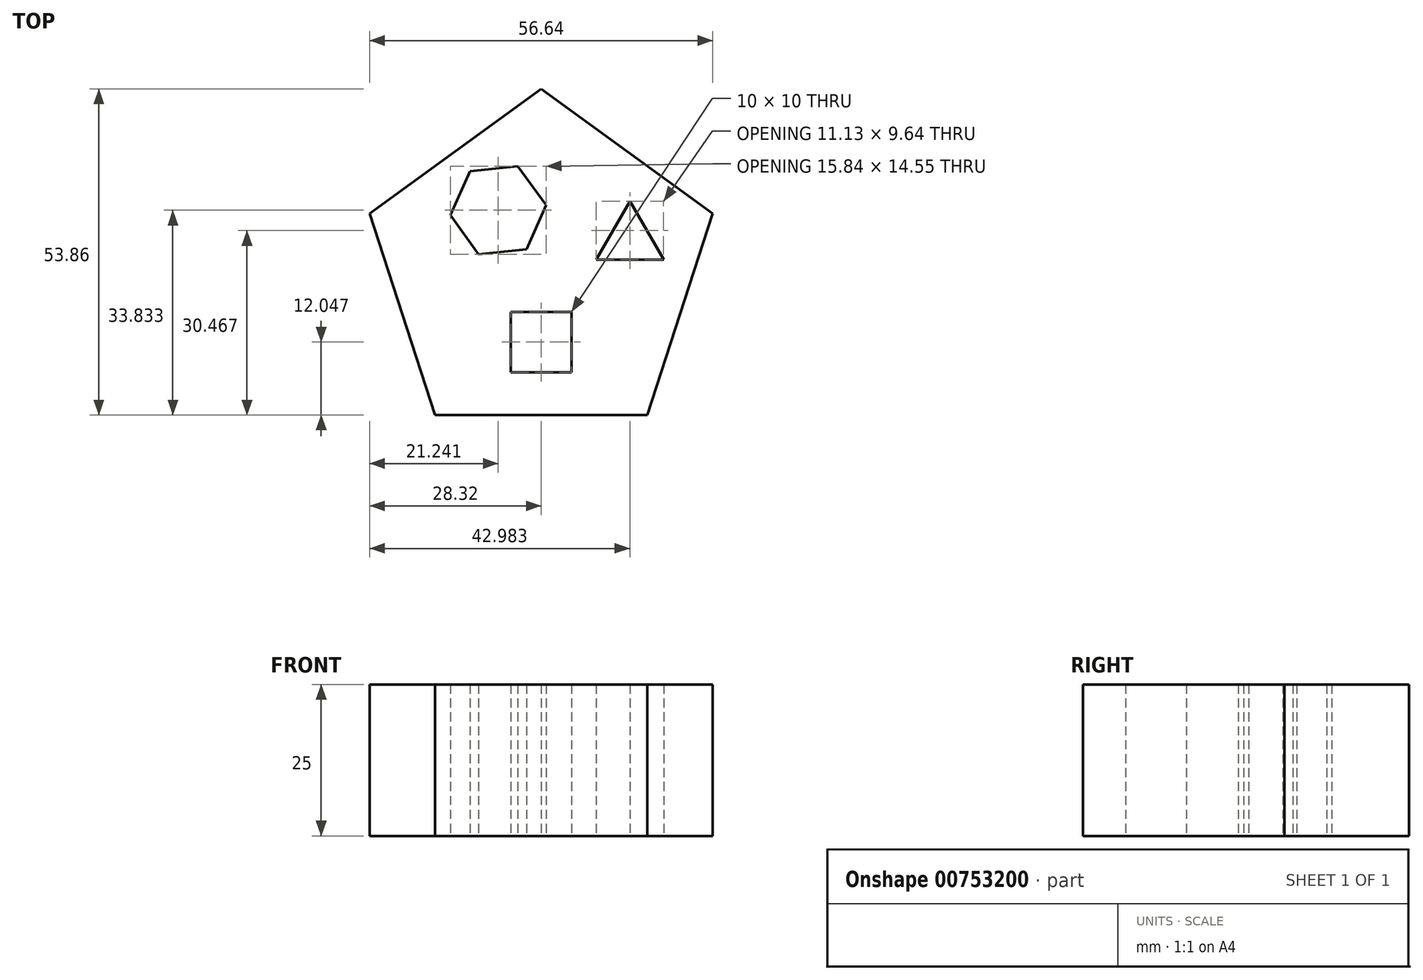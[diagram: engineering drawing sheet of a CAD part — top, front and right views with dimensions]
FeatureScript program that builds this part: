
annotation { "Feature Type Name" : "Feature", "Feature Type Description" : "" }
export const myFeature = defineFeature(function(context is Context, id is Id, definition is map)
    precondition{}
    {
        {
            var Q0;
            Q0=qCreatedBy(makeId("Top.planeOp"),FACE);
            var sketch = newSketch(context, id + "F0", { "sketchPlane" : qUnion([Q0])});
            skCircle(sketch, "E0.cCircle", {"center": v(0, 0) * mm, "radius": 24.09 * mm, "construction": true});
            skLineSegment(sketch, "E0.0", {"start": v(28.32, 9.2) * mm, "end": v(17.5, -24.09) * mm});
            skLineSegment(sketch, "E0.1", {"start": v(17.5, -24.09) * mm, "end": v(-17.5, -24.09) * mm});
            skLineSegment(sketch, "E0.2", {"start": v(-17.5, -24.09) * mm, "end": v(-28.32, 9.2) * mm});
            skLineSegment(sketch, "E0.3", {"start": v(-28.32, 9.2) * mm, "end": v(0, 29.77) * mm});
            skLineSegment(sketch, "E0.4", {"start": v(0, 29.77) * mm, "end": v(28.32, 9.2) * mm});
            skPoint(sketch, "E0.0.midPoint", {"position": v(22.9, -7.44) * mm});
            skLineSegment(sketch, "E1.bottom", {"start": v(5, -17.04) * mm, "end": v(-5, -17.04) * mm});
            skLineSegment(sketch, "E1.top", {"start": v(5, -7.04) * mm, "end": v(-5, -7.04) * mm});
            skLineSegment(sketch, "E1.left", {"start": v(5, -17.04) * mm, "end": v(5, -7.04) * mm});
            skLineSegment(sketch, "E1.right", {"start": v(-5, -17.04) * mm, "end": v(-5, -7.04) * mm});
            skPoint(sketch, "E1.middle", {"position": v(0, -12.04) * mm});
            skLineSegment(sketch, "E2", {"start": v(0, 0) * mm, "end": v(0, -24.09) * mm, "construction": true});
            skCircle(sketch, "E3.cCircle", {"center": v(-7.08, 9.74) * mm, "radius": 6.9 * mm, "construction": true});
            skLineSegment(sketch, "E3.0", {"start": v(-10.32, 2.47) * mm, "end": v(-15, 8.91) * mm});
            skLineSegment(sketch, "E3.1", {"start": v(-15, 8.91) * mm, "end": v(-11.76, 16.19) * mm});
            skLineSegment(sketch, "E3.2", {"start": v(-11.76, 16.19) * mm, "end": v(-3.84, 17.02) * mm});
            skLineSegment(sketch, "E3.3", {"start": v(-3.84, 17.02) * mm, "end": v(0.84, 10.58) * mm});
            skLineSegment(sketch, "E3.4", {"start": v(0.84, 10.58) * mm, "end": v(-2.4, 3.3) * mm});
            skLineSegment(sketch, "E3.5", {"start": v(-2.4, 3.3) * mm, "end": v(-10.32, 2.47) * mm});
            skPoint(sketch, "E3.0.midPoint", {"position": v(-12.66, 5.69) * mm});
            skLineSegment(sketch, "E4", {"start": v(0, 0) * mm, "end": v(-14.16, 19.49) * mm, "construction": true});
            skLineSegment(sketch, "E5", {"start": v(0, 0) * mm, "end": v(28.32, 9.2) * mm, "construction": true});
            skCircle(sketch, "E6.cCircle", {"center": v(14.66, 4.77) * mm, "radius": 3.21 * mm, "construction": true});
            skLineSegment(sketch, "E6.0", {"start": v(20.23, 1.56) * mm, "end": v(9.1, 1.56) * mm});
            skLineSegment(sketch, "E6.1", {"start": v(9.1, 1.56) * mm, "end": v(14.66, 11.2) * mm});
            skLineSegment(sketch, "E6.2", {"start": v(14.66, 11.2) * mm, "end": v(20.23, 1.56) * mm});
            skPoint(sketch, "E6.0.midPoint", {"position": v(14.66, 1.56) * mm});
            skSolve(sketch);
        }
        {
            var Q0;
            Q0 = qSketchRegion(id + "F0", true);
            extrude(context, id + "F1", {"entities" : qUnion([Q0]), "depth" : 25 * mm, "offsetDistance" : 25 * mm});
        }
    });
